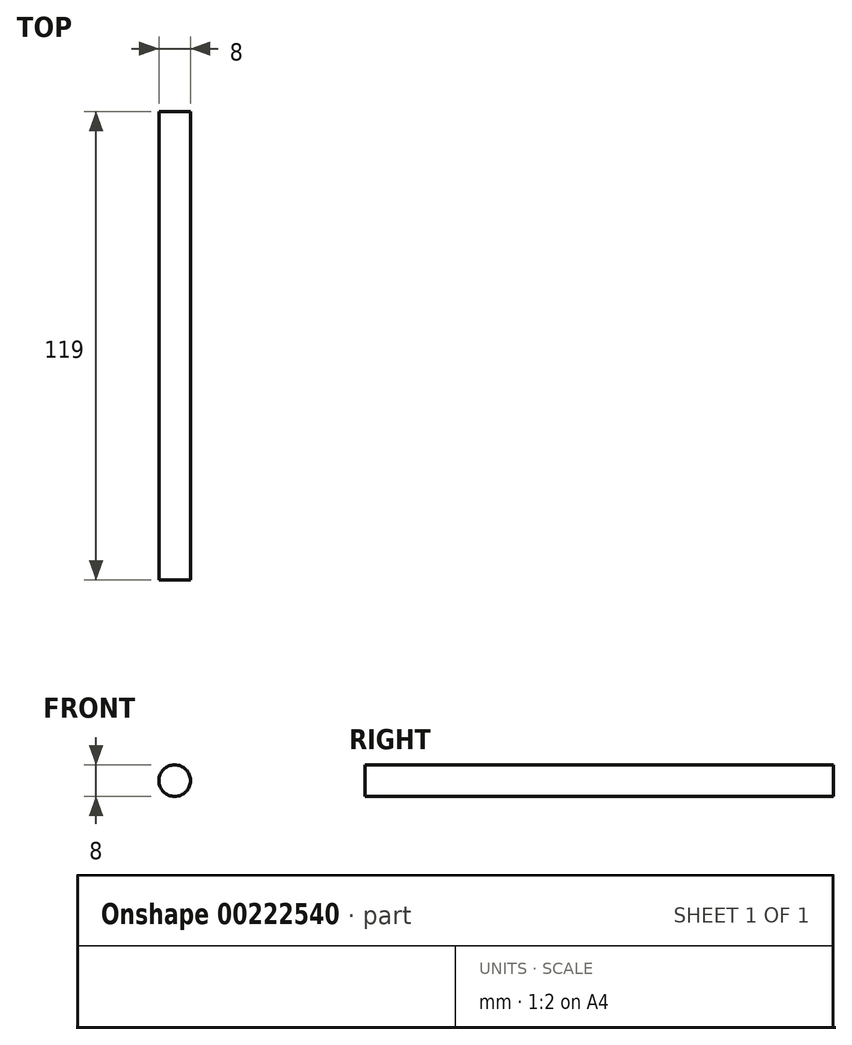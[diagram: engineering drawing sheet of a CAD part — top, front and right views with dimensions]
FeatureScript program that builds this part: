
annotation { "Feature Type Name" : "Feature", "Feature Type Description" : "" }
export const myFeature = defineFeature(function(context is Context, id is Id, definition is map)
    precondition{}
    {
        {
            var Q0;
            Q0=qCreatedBy(makeId("Front.planeOp"),FACE);
            var sketch = newSketch(context, id + "F0", { "sketchPlane" : qUnion([Q0])});
            skCircle(sketch, "E0", {"center": v(0, 0) * mm, "radius": 4 * mm});
            skSolve(sketch);
        }
        {
            var Q0;
            Q0 = qSketchRegion(id + "F0", true);
            extrude(context, id + "F1", {"entities" : qUnion([Q0]), "depth" : 119 * mm});
        }
    });
